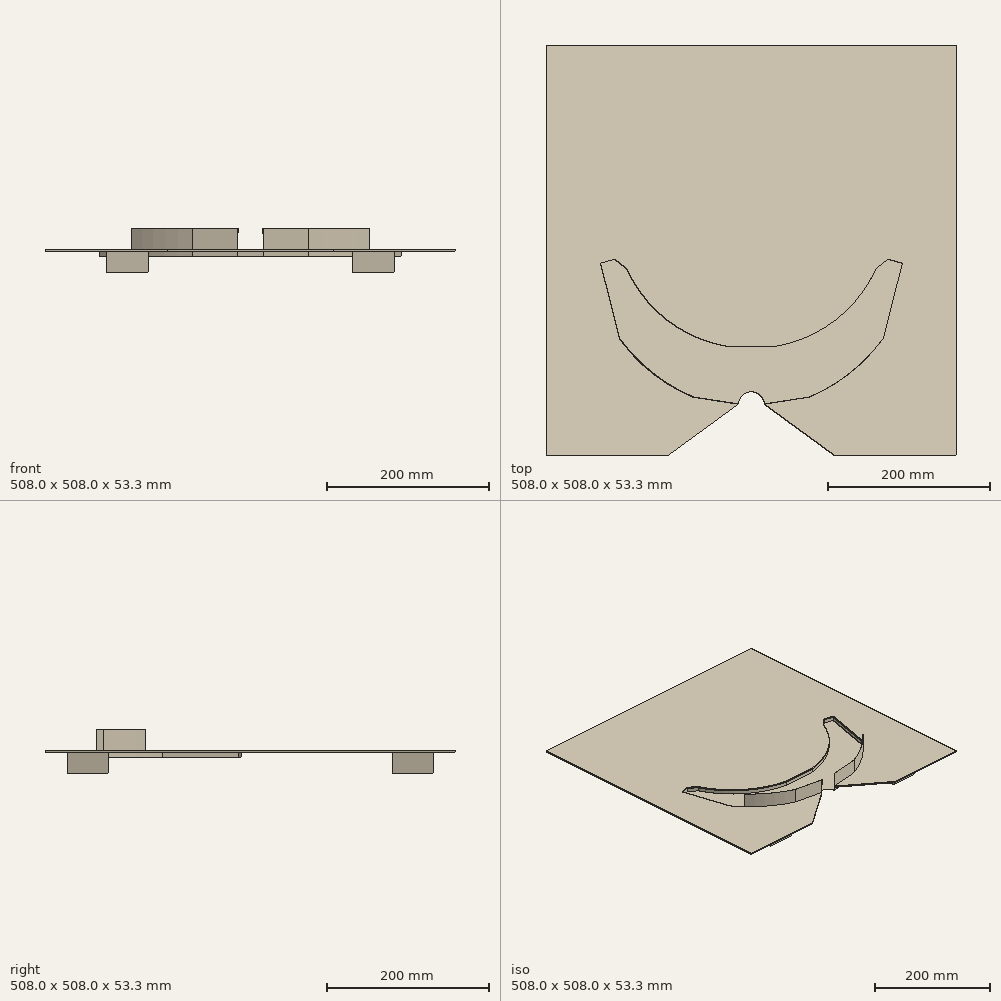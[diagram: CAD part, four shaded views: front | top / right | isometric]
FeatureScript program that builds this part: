
annotation { "Feature Type Name" : "Feature", "Feature Type Description" : "" }
export const myFeature = defineFeature(function(context is Context, id is Id, definition is map)
    precondition{}
    {
        {
            var Q0;
            Q0=qCreatedBy(makeId("Top.planeOp"),FACE);
            var sketch = newSketch(context, id + "F0", { "sketchPlane" : qUnion([Q0])});
            skLineSegment(sketch, "E0", {"start": v(-137.28, 47.77) * mm, "end": v(-122.4, 35.87) * mm});
            skPoint(sketch, "E1.visualSharp", {"position": v(-81.15, -27.88) * mm});
            skArc(sketch, "E2", {"start": v(-122.4, 35.87) * mm, "mid": v(-73.13, -27.17) * mm, "end": v(0, -59.64) * mm});
            skLineSegment(sketch, "E3", {"start": v(0, -59.64) * mm, "end": v(31.75, -59.64) * mm});
            skLineSegment(sketch, "E4", {"start": v(-137.28, 47.77) * mm, "end": v(-155.74, 43.07) * mm});
            skLineSegment(sketch, "E5", {"start": v(-155.74, 43.07) * mm, "end": v(-131.84, -50.77) * mm});
            skArc(sketch, "E6", {"start": v(-131.84, -50.77) * mm, "mid": v(-91.18, -93.2) * mm, "end": v(-40.6, -123.14) * mm});
            skLineSegment(sketch, "E7", {"start": v(-40.6, -123.14) * mm, "end": v(15.88, -131.94) * mm});
            skPoint(sketch, "E7.endSnap0", {"position": v(15.87, -59.64) * mm});
            skLineSegment(sketch, "E8", {"start": v(15.88, -131.94) * mm, "end": v(31.75, -131.94) * mm});
            skLineSegment(sketch, "E9.MirrorCS", {"start": v(63.5, -59.64) * mm, "end": v(31.75, -59.64) * mm});
            skArc(sketch, "E10.MirrorCS", {"start": v(185.9, 35.87) * mm, "mid": v(136.63, -27.17) * mm, "end": v(63.5, -59.64) * mm});
            skLineSegment(sketch, "E11.MirrorCS", {"start": v(200.78, 47.77) * mm, "end": v(185.9, 35.87) * mm});
            skLineSegment(sketch, "E12.MirrorCS", {"start": v(200.78, 47.77) * mm, "end": v(219.24, 43.07) * mm});
            skLineSegment(sketch, "E13.MirrorCS", {"start": v(219.24, 43.07) * mm, "end": v(195.34, -50.77) * mm});
            skArc(sketch, "E14.MirrorCS", {"start": v(195.34, -50.77) * mm, "mid": v(154.68, -93.2) * mm, "end": v(104.1, -123.14) * mm});
            skLineSegment(sketch, "E15.MirrorCS", {"start": v(104.1, -123.14) * mm, "end": v(47.62, -131.94) * mm});
            skLineSegment(sketch, "E16.MirrorCS", {"start": v(47.62, -131.94) * mm, "end": v(31.75, -131.94) * mm});
            skSolve(sketch);
        }
        {
            var Q0;
            Q0 = qSketchRegion(id + "F0", true);
            extrude(context, id + "F1", {"entities" : qUnion([Q0]), "depth" : 25.4 * mm});
        }
        {
            var Q0;
            Q0=qCreatedBy(makeId("Top.planeOp"),FACE);
            var sketch = newSketch(context, id + "F2", { "sketchPlane" : qUnion([Q0])});
            skLineSegment(sketch, "E17.bottom", {"start": v(-222.25, -195.44) * mm, "end": v(285.75, -195.44) * mm});
            skLineSegment(sketch, "E17.top", {"start": v(-222.25, 312.56) * mm, "end": v(285.75, 312.56) * mm});
            skLineSegment(sketch, "E17.left", {"start": v(-222.25, -195.44) * mm, "end": v(-222.25, 312.56) * mm});
            skLineSegment(sketch, "E17.right", {"start": v(285.75, -195.44) * mm, "end": v(285.75, 312.56) * mm});
            skLineSegment(sketch, "E18", {"start": v(285.75, -131.94) * mm, "end": v(-222.25, -131.94) * mm});
            skSolve(sketch);
        }
        {
            var Q0;
            Q0 = qSketchRegion(id + "F2", true);
            extrude(context, id + "F3", {"entities" : qUnion([Q0]), "operationType" : NewBodyOperationType.ADD, "oppositeDirection" : true, "depth" : 2.54 * mm});
        }
        {
            var Q0;
            Q0=makeQuery(id+"F1.opExtrude","CAP_FACE",FACE,{"disambiguationData":[OSD([sQuery(id+"F0.wireOp",EDGE,"E0"),sQuery(id+"F0.wireOp",EDGE,"E2"),sQuery(id+"F0.wireOp",EDGE,"E3"),sQuery(id+"F0.wireOp",EDGE,"hnqgBd3M-qgem-e8SO-lxSi-6uIqIVxK64Ht"),sQuery(id+"F0.wireOp",EDGE,"E4"),sQuery(id+"F0.wireOp",EDGE,"E5"),sQuery(id+"F0.wireOp",EDGE,"E6"),sQuery(id+"F0.wireOp",EDGE,"e01b028b-e6ec-4f8b-8a67-21f2058a65fc0.MirrorCS"),sQuery(id+"F0.wireOp",EDGE,"e01b028b-e6ec-4f8b-8a67-21f2058a65fc1.MirrorCS"),sQuery(id+"F0.wireOp",EDGE,"e01b028b-e6ec-4f8b-8a67-21f2058a65fc2.MirrorCS"),sQuery(id+"F0.wireOp",EDGE,"e01b028b-e6ec-4f8b-8a67-21f2058a65fc3.MirrorCS"),sQuery(id+"F0.wireOp",EDGE,"e01b028b-e6ec-4f8b-8a67-21f2058a65fc5.MirrorCS"),sQuery(id+"F0.wireOp",EDGE,"dbc7e001-0156-497f-aec9-f0f8cc6767f40.MirrorCS"),sQuery(id+"F0.wireOp",EDGE,"f19cee15-525d-412a-ac4d-8334f70f2a060.MirrorCS")])],"isStart":false});
            extrude(context, id + "F4", {"entities" : qUnion([Q0]), "operationType" : NewBodyOperationType.ADD, "oppositeDirection" : true, "depth" : 34.3 * mm});
        }
        {
            var Q0;
            Q0=makeQuery(id+"F1.opExtrude","CAP_FACE",FACE,{"disambiguationData":[OSD([sQuery(id+"F0.wireOp",EDGE,"E0"),sQuery(id+"F0.wireOp",EDGE,"E2"),sQuery(id+"F0.wireOp",EDGE,"E3"),sQuery(id+"F0.wireOp",EDGE,"hnqgBd3M-qgem-e8SO-lxSi-6uIqIVxK64Ht"),sQuery(id+"F0.wireOp",EDGE,"E4"),sQuery(id+"F0.wireOp",EDGE,"E5"),sQuery(id+"F0.wireOp",EDGE,"E6"),sQuery(id+"F0.wireOp",EDGE,"e01b028b-e6ec-4f8b-8a67-21f2058a65fc0.MirrorCS"),sQuery(id+"F0.wireOp",EDGE,"e01b028b-e6ec-4f8b-8a67-21f2058a65fc1.MirrorCS"),sQuery(id+"F0.wireOp",EDGE,"e01b028b-e6ec-4f8b-8a67-21f2058a65fc2.MirrorCS"),sQuery(id+"F0.wireOp",EDGE,"e01b028b-e6ec-4f8b-8a67-21f2058a65fc3.MirrorCS"),sQuery(id+"F0.wireOp",EDGE,"e01b028b-e6ec-4f8b-8a67-21f2058a65fc5.MirrorCS"),sQuery(id+"F0.wireOp",EDGE,"dbc7e001-0156-497f-aec9-f0f8cc6767f40.MirrorCS"),sQuery(id+"F0.wireOp",EDGE,"f19cee15-525d-412a-ac4d-8334f70f2a060.MirrorCS")])],"isStart":false});
            shell(context, id + "F5", {"entities" : qUnion([Q0]), "thickness" : 0.25 * mm});
        }
        {
            var Q0;
            Q0=makeQuery(id+"F3.opExtrude","CAP_FACE",FACE,{"disambiguationData":[OSD([sQuery(id+"F2.wireOp",EDGE,"E17.bottom"),sQuery(id+"F2.wireOp",EDGE,"E17.top"),sQuery(id+"F2.wireOp",EDGE,"E17.left"),sQuery(id+"F2.wireOp",EDGE,"E17.right")])],"isStart":false});
            var sketch = newSketch(context, id + "F6", { "sketchPlane" : qUnion([Q0])});
            skLineSegment(sketch, "E19.bottom", {"start": v(-146.05, -284.86) * mm, "end": v(-95.25, -284.86) * mm});
            skLineSegment(sketch, "E19.top", {"start": v(-146.05, -234.06) * mm, "end": v(-95.25, -234.06) * mm});
            skLineSegment(sketch, "E19.left", {"start": v(-146.05, -284.86) * mm, "end": v(-146.05, -234.06) * mm});
            skLineSegment(sketch, "E19.right", {"start": v(-95.25, -284.86) * mm, "end": v(-95.25, -234.06) * mm});
            skLineSegment(sketch, "E20.bottom", {"start": v(158.75, -284.86) * mm, "end": v(209.55, -284.86) * mm});
            skLineSegment(sketch, "E20.top", {"start": v(158.75, -234.06) * mm, "end": v(209.55, -234.06) * mm});
            skLineSegment(sketch, "E20.left", {"start": v(158.75, -284.86) * mm, "end": v(158.75, -234.06) * mm});
            skLineSegment(sketch, "E20.right", {"start": v(209.55, -284.86) * mm, "end": v(209.55, -234.06) * mm});
            skLineSegment(sketch, "E21", {"start": v(-222.25, -58.56) * mm, "end": v(285.75, -58.56) * mm});
            skLineSegment(sketch, "E22.MirrorCS", {"start": v(158.75, 167.75) * mm, "end": v(158.75, 116.95) * mm});
            skLineSegment(sketch, "E23.MirrorCS", {"start": v(158.75, 167.75) * mm, "end": v(209.55, 167.75) * mm});
            skLineSegment(sketch, "E24.MirrorCS", {"start": v(158.75, 116.95) * mm, "end": v(209.55, 116.95) * mm});
            skLineSegment(sketch, "E25.MirrorCS", {"start": v(-146.05, 167.75) * mm, "end": v(-146.05, 116.95) * mm});
            skLineSegment(sketch, "E26.MirrorCS", {"start": v(209.55, 167.75) * mm, "end": v(209.55, 116.95) * mm});
            skLineSegment(sketch, "E27.MirrorCS", {"start": v(-146.05, 116.95) * mm, "end": v(-95.25, 116.95) * mm});
            skLineSegment(sketch, "E28.MirrorCS", {"start": v(-95.25, 167.75) * mm, "end": v(-95.25, 116.95) * mm});
            skLineSegment(sketch, "E29.MirrorCS", {"start": v(-146.05, 167.75) * mm, "end": v(-95.25, 167.75) * mm});
            skSolve(sketch);
        }
        {
            var Q0;
            Q0 = qSketchRegion(id + "F6", true);
            extrude(context, id + "F7", {"entities" : qUnion([Q0]), "operationType" : NewBodyOperationType.ADD, "depth" : 25.4 * mm});
        }
        {
            var Q0;
            Q0=qCreatedBy(makeId("Front.planeOp"),FACE);
            var sketch = newSketch(context, id + "F8", { "sketchPlane" : qUnion([Q0])});
            skLineSegment(sketch, "E30.bottom", {"start": v(232.39, 0) * mm, "end": v(-156.65, 0) * mm});
            skLineSegment(sketch, "E30.top", {"start": v(232.39, 108.88) * mm, "end": v(-156.65, 108.88) * mm});
            skLineSegment(sketch, "E30.left", {"start": v(232.39, 0) * mm, "end": v(232.39, 108.88) * mm});
            skLineSegment(sketch, "E30.right", {"start": v(-156.65, 0) * mm, "end": v(-156.65, 108.88) * mm});
            skSolve(sketch);
        }
        {
            var Q0;
            Q0 = qSketchRegion(id + "F8", true);
            extrude(context, id + "F9", {"entities" : qUnion([Q0]), "operationType" : NewBodyOperationType.REMOVE, "oppositeDirection" : true, "depth" : 169.67 * mm, "hasSecondDirection" : true, "secondDirectionOppositeDirection" : false, "secondDirectionDepth" : 71.12 * mm});
        }
        {
            var Q0;
            Q0=makeQuery(id+"F9.boolean.opBoolean","MERGE",FACE,{"derivedFrom":[makeQuery(id+"F3.opExtrude","CAP_FACE",FACE,{"disambiguationData":[OSD([sQuery(id+"F2.wireOp",EDGE,"E17.bottom"),sQuery(id+"F2.wireOp",EDGE,"E17.top"),sQuery(id+"F2.wireOp",EDGE,"E17.left"),sQuery(id+"F2.wireOp",EDGE,"E17.right")])],"isStart":true}),makeQuery(id+"F9.opExtrude","SWEPT_FACE",FACE,{"disambiguationData":[OSD([sQuery(id+"F8.wireOp",EDGE,"E30.bottom")])]})]});
            var sketch = newSketch(context, id + "F10", { "sketchPlane" : qUnion([Q0])});
            skCircle(sketch, "E31", {"center": v(31.75, -131.94) * mm, "radius": 15.88 * mm});
            skSolve(sketch);
        }
        {
            var Q0;
            Q0 = qSketchRegion(id + "F10", true);
            var Q1;
            Q1=makeQuery(id+"F3.opExtrude","CAP_EDGE",EDGE,{"disambiguationData":[OSD([sQuery(id+"F2.wireOp",EDGE,"E17.bottom")])],"isStart":true});
            revolve(context, id + "F11", {"operationType" : NewBodyOperationType.REMOVE, "entities" : qUnion([Q0]), "axis" : qUnion([Q1]), "revolveType" : RevolveType.FULL});
        }
        {
            var Q0;
            Q0=makeQuery(id+"F9.boolean.opBoolean","MERGE",FACE,{"derivedFrom":[makeQuery(id+"F3.opExtrude","CAP_FACE",FACE,{"disambiguationData":[OSD([sQuery(id+"F2.wireOp",EDGE,"E17.bottom"),sQuery(id+"F2.wireOp",EDGE,"E17.top"),sQuery(id+"F2.wireOp",EDGE,"E17.left"),sQuery(id+"F2.wireOp",EDGE,"E17.right")])],"isStart":true}),makeQuery(id+"F9.opExtrude","SWEPT_FACE",FACE,{"disambiguationData":[OSD([sQuery(id+"F8.wireOp",EDGE,"E30.bottom")])]})]});
            var sketch = newSketch(context, id + "F12", { "sketchPlane" : qUnion([Q0])});
            skLineSegment(sketch, "E32", {"start": v(15.88, -131.94) * mm, "end": v(-71.1, -195.44) * mm});
            skLineSegment(sketch, "E33.MirrorCS", {"start": v(47.62, -131.94) * mm, "end": v(134.6, -195.44) * mm});
            skSolve(sketch);
        }
        {
            var Q0;
            {var subQ0=sQuery(id+"F12.wireOp",EDGE,"E32");Q0=makeQuery(id+"F12.imprint","IMPRINT",FACE,{"disambiguationData":[TD([[makeQuery(id+"F12.imprint","IMPRINT",EDGE,{"derivedFrom":subQ0}),1.0]])]});}
            extrude(context, id + "F13", {"entities" : qUnion([Q0]), "operationType" : NewBodyOperationType.REMOVE, "oppositeDirection" : true, "depth" : 2.8 * mm});
        }
    });
